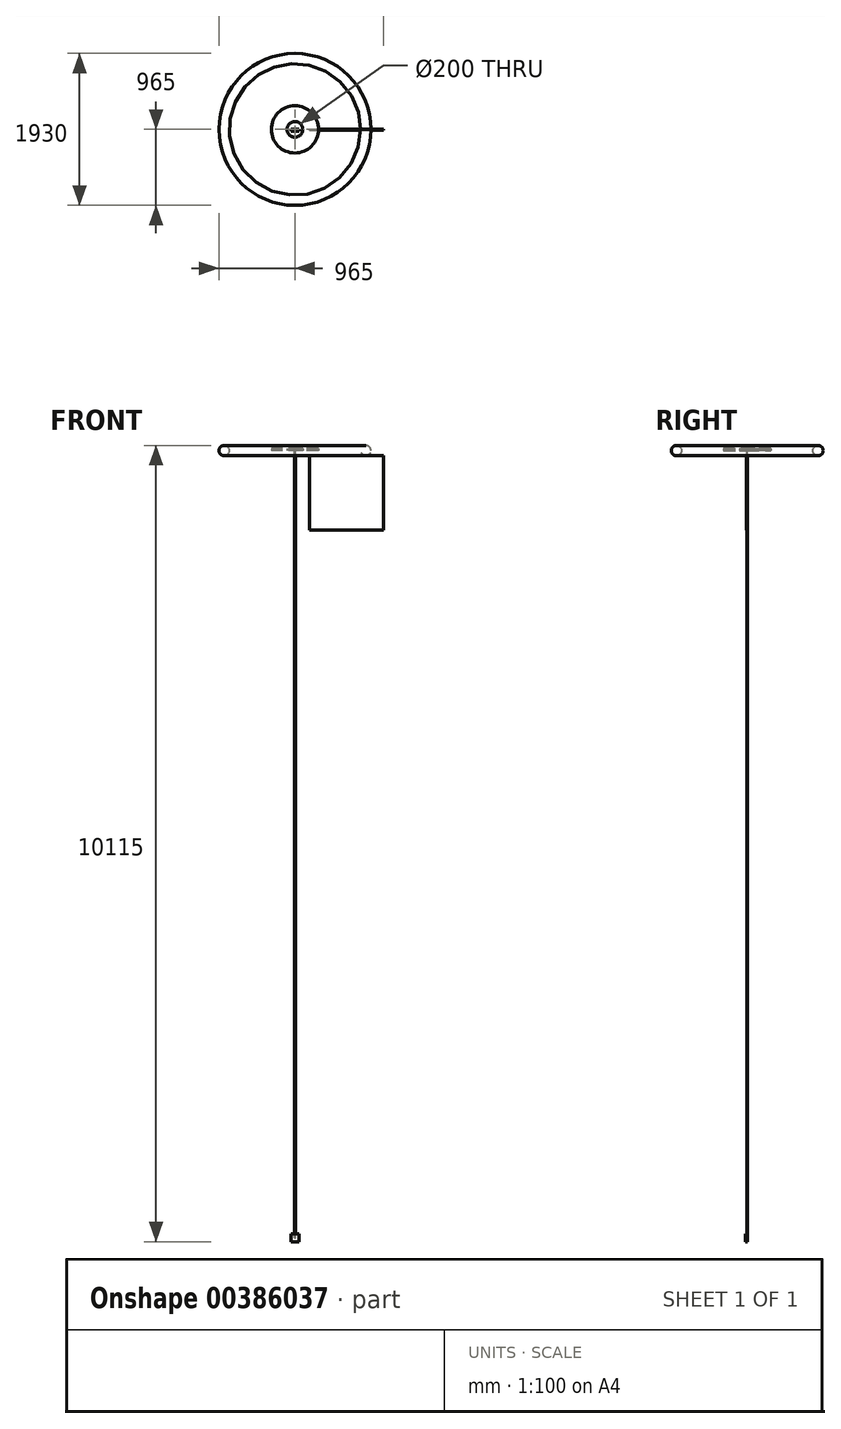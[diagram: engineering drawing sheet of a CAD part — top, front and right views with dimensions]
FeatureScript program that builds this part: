
annotation { "Feature Type Name" : "Feature", "Feature Type Description" : "" }
export const myFeature = defineFeature(function(context is Context, id is Id, definition is map)
    precondition{}
    {
        {
            var Q0;
            Q0=qCreatedBy(makeId("Front.planeOp"),FACE);
            var sketch = newSketch(context, id + "F0", { "sketchPlane" : qUnion([Q0])});
            skCircle(sketch, "E0", {"center": v(900, 0) * mm, "radius": 65 * mm});
            skLineSegment(sketch, "E1", {"start": v(0, 0) * mm, "end": v(900, 0) * mm, "construction": true});
            skLineSegment(sketch, "E2", {"start": v(0, 0) * mm, "end": v(0, -444.82) * mm, "construction": true});
            skSolve(sketch);
        }
        {
            var Q0;
            Q0=makeQuery(id+"F0.imprint","IMPRINT",FACE,{"disambiguationData":[TD([[makeQuery(id+"F0.imprint","IMPRINT",EDGE,{"derivedFrom":sQuery(id+"F0.wireOp",EDGE,"E0")}),1.0]])]});
            var Q1;
            Q1=sQuery(id+"F0.wireOp",EDGE,"E2");
            revolve(context, id + "F1", {"entities" : qUnion([Q0]), "axis" : qUnion([Q1]), "revolveType" : RevolveType.FULL});
        }
        {
            var Q0;
            Q0=qCreatedBy(makeId("Top.planeOp"),FACE);
            var sketch = newSketch(context, id + "F2", { "sketchPlane" : qUnion([Q0])});
            skCircle(sketch, "E3", {"center": v(0, 0) * mm, "radius": 5 * mm});
            skSolve(sketch);
        }
        {
            var Q0;
            Q0=makeQuery(id+"F2.imprint","IMPRINT",FACE,{"disambiguationData":[TD([[makeQuery(id+"F2.imprint","IMPRINT",EDGE,{"derivedFrom":sQuery(id+"F2.wireOp",EDGE,"E3")}),1.0]])]});
            extrude(context, id + "F3", {"entities" : qUnion([Q0]), "oppositeDirection" : true, "depth" : 10000 * mm});
        }
        {
            var Q0;
            Q0=qCreatedBy(makeId("Top.planeOp"),FACE);
            var sketch = newSketch(context, id + "F4", { "sketchPlane" : qUnion([Q0])});
            skCircle(sketch, "E4", {"center": v(0, 0) * mm, "radius": 300 * mm});
            skCircle(sketch, "E5", {"center": v(0, 0) * mm, "radius": 100 * mm});
            skSolve(sketch);
        }
        {
            var Q0;
            Q0=makeQuery(id+"F4.imprint","IMPRINT",FACE,{"disambiguationData":[TD([[makeQuery(id+"F4.imprint","IMPRINT",EDGE,{"derivedFrom":sQuery(id+"F4.wireOp",EDGE,"E4")}),1.0]])]});
            extrude(context, id + "F5", {"entities" : qUnion([Q0]), "operationType" : NewBodyOperationType.ADD, "depth" : 25 * mm});
        }
        {
            var Q0;
            Q0=qCreatedBy(makeId("Front.planeOp"),FACE);
            var sketch = newSketch(context, id + "F6", { "sketchPlane" : qUnion([Q0])});
            skLineSegment(sketch, "E6.bottom", {"start": v(185.51, -65.18) * mm, "end": v(1127.51, -65.18) * mm});
            skLineSegment(sketch, "E6.top", {"start": v(185.51, -1007.18) * mm, "end": v(1127.51, -1007.18) * mm});
            skLineSegment(sketch, "E6.left", {"start": v(185.51, -65.18) * mm, "end": v(185.51, -1007.18) * mm});
            skLineSegment(sketch, "E6.right", {"start": v(1127.51, -65.18) * mm, "end": v(1127.51, -1007.18) * mm});
            skSolve(sketch);
        }
        {
            var Q0;
            Q0=makeQuery(id+"F6.imprint","IMPRINT",FACE,{"disambiguationData":[TD([[makeQuery(id+"F6.imprint","IMPRINT",EDGE,{"derivedFrom":sQuery(id+"F6.wireOp",EDGE,"E6.bottom")}),-1.0]])]});
            extrude(context, id + "F7", {"entities" : qUnion([Q0]), "operationType" : NewBodyOperationType.ADD, "depth" : 10 * mm});
        }
        {
            var Q0;
            Q0=qCreatedBy(makeId("Front.planeOp"),FACE);
            var sketch = newSketch(context, id + "F8", { "sketchPlane" : qUnion([Q0])});
            skLineSegment(sketch, "E7.bottom", {"start": v(50, -10050) * mm, "end": v(-50, -10050) * mm});
            skLineSegment(sketch, "E7.top", {"start": v(50, -9950) * mm, "end": v(-50, -9950) * mm});
            skLineSegment(sketch, "E7.left", {"start": v(50, -10050) * mm, "end": v(50, -9950) * mm});
            skLineSegment(sketch, "E7.right", {"start": v(-50, -10050) * mm, "end": v(-50, -9950) * mm});
            skPoint(sketch, "E7.middle", {"position": v(0, -10000) * mm});
            skSolve(sketch);
        }
        {
            var Q0;
            Q0=makeQuery(id+"F8.imprint","IMPRINT",FACE,{"disambiguationData":[TD([[makeQuery(id+"F8.imprint","IMPRINT",EDGE,{"derivedFrom":sQuery(id+"F8.wireOp",EDGE,"E7.bottom")}),-1.0]])]});
            extrude(context, id + "F9", {"entities" : qUnion([Q0]), "operationType" : NewBodyOperationType.ADD, "depth" : 25 * mm});
        }
    });
